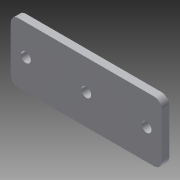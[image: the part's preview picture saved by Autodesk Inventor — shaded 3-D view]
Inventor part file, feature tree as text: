
AUTODESK INVENTOR PART (.ipt)
format: ipt  version: 2014 (Build 180170000, 170)  size: 88,576 bytes
history: native  units: in
note: dims shown in document units (in); Inventor stores cm internally (conversion verified against a paired STEP export)
features: extrude x1, sketch x1
ambient origin geometry x8: Origin, YZ Plane, XZ Plane, XY Plane, X Axis, Y Axis, Z Axis, Center Point
bodies: Solid1 (feature_tree)
feature tree (2):
  extrude  "Extrusion1"  Depth=1.0in
  sketch  "Sketch1"  dims[d0=2.5in d1=1.0in d2=0.25in d3=0.163in d4=1.1811in d6=1.0in d7=0.3937in d9=1.0in d11=0.125in d12=0.125in d13=0.0in]
